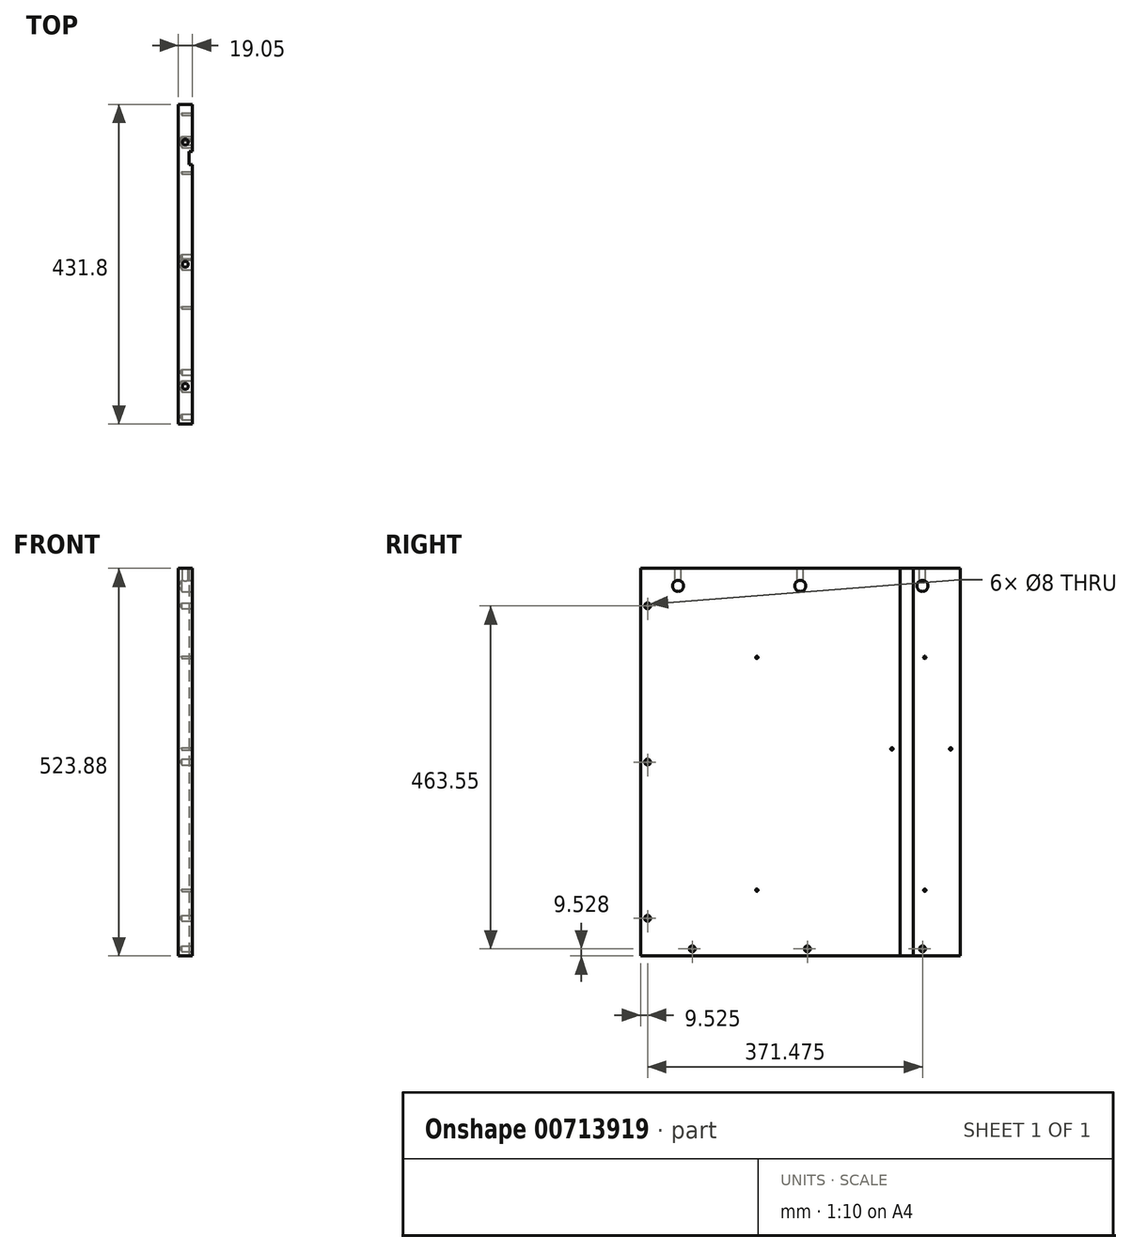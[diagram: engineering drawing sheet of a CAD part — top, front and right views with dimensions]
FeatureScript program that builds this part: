
annotation { "Feature Type Name" : "Feature", "Feature Type Description" : "" }
export const myFeature = defineFeature(function(context is Context, id is Id, definition is map)
    precondition{}
    {
        {
            var Q0;
            Q0=qCreatedBy(makeId("Right.planeOp"),FACE);
            var sketch = newSketch(context, id + "F0", { "sketchPlane" : qUnion([Q0])});
            skLineSegment(sketch, "E0.bottom", {"start": v(215.9, 261.94) * mm, "end": v(-215.9, 261.94) * mm});
            skLineSegment(sketch, "E0.top", {"start": v(215.9, -261.94) * mm, "end": v(-215.9, -261.94) * mm});
            skLineSegment(sketch, "E0.left", {"start": v(215.9, 261.94) * mm, "end": v(215.9, -261.94) * mm});
            skLineSegment(sketch, "E0.right", {"start": v(-215.9, 261.94) * mm, "end": v(-215.9, -261.94) * mm});
            skPoint(sketch, "E0.middle", {"position": v(0, 0) * mm});
            skSolve(sketch);
        }
        {
            var Q0;
            Q0=makeQuery(id+"F0.imprint","IMPRINT",FACE,{"disambiguationData":[TD([[makeQuery(id+"F0.imprint","IMPRINT",EDGE,{"derivedFrom":sQuery(id+"F0.wireOp",EDGE,"E0.bottom")}),1.0]])]});
            extrude(context, id + "F1", {"entities" : qUnion([Q0]), "depth" : 19.05 * mm, "offsetDistance" : 25.4 * mm});
        }
        {
            var Q0;
            Q0=makeQuery(id+"F1.opExtrude","CAP_FACE",FACE,{"disambiguationData":[OSD([sQuery(id+"F0.wireOp",EDGE,"E0.bottom"),sQuery(id+"F0.wireOp",EDGE,"E0.top"),sQuery(id+"F0.wireOp",EDGE,"E0.left"),sQuery(id+"F0.wireOp",EDGE,"E0.right")])],"isStart":false});
            var sketch = newSketch(context, id + "F2", { "sketchPlane" : qUnion([Q0])});
            skLineSegment(sketch, "E1", {"start": v(-215.9, 261.94) * mm, "end": v(-215.9, 238.06) * mm});
            skLineSegment(sketch, "E2", {"start": v(-215.9, 238.06) * mm, "end": v(215.9, 238.06) * mm});
            skLineSegment(sketch, "E3", {"start": v(215.9, 261.94) * mm, "end": v(206.38, 261.94) * mm});
            skPoint(sketch, "E4", {"position": v(206.38, 0) * mm});
            skPoint(sketch, "E5", {"position": v(206.38, -211.14) * mm});
            skLineSegment(sketch, "E6", {"start": v(-215.9, -261.94) * mm, "end": v(-215.9, -252.41) * mm});
            skLineSegment(sketch, "E7", {"start": v(-215.9, -252.41) * mm, "end": v(215.9, -252.41) * mm});
            skLineSegment(sketch, "E8", {"start": v(215.9, -252.41) * mm, "end": v(165.1, -252.41) * mm});
            skLineSegment(sketch, "E9", {"start": v(-215.9, -252.41) * mm, "end": v(-146.05, -252.41) * mm});
            skLineSegment(sketch, "E10", {"start": v(-215.9, -252.41) * mm, "end": v(-9.53, -252.41) * mm});
            skPoint(sketch, "E11", {"position": v(-146.05, -252.41) * mm});
            skPoint(sketch, "E12", {"position": v(-9.53, -252.41) * mm});
            skPoint(sketch, "E13", {"position": v(165.1, -252.41) * mm});
            skLineSegment(sketch, "E14", {"start": v(-215.9, 238.06) * mm, "end": v(-165.1, 238.06) * mm});
            skLineSegment(sketch, "E15", {"start": v(215.9, 238.06) * mm, "end": v(165.1, 238.06) * mm});
            skLineSegment(sketch, "E16", {"start": v(0, 238.06) * mm, "end": v(0, 261.94) * mm});
            skPoint(sketch, "E17", {"position": v(-165.1, 238.06) * mm});
            skPoint(sketch, "E18", {"position": v(0, 238.06) * mm});
            skPoint(sketch, "E19", {"position": v(165.1, 238.06) * mm});
            skLineSegment(sketch, "E20", {"start": v(215.9, -252.41) * mm, "end": v(9.52, -252.41) * mm});
            skPoint(sketch, "E21", {"position": v(9.52, -252.41) * mm});
            skLineSegment(sketch, "E22", {"start": v(-215.9, 261.94) * mm, "end": v(-206.38, 261.94) * mm});
            skLineSegment(sketch, "E23", {"start": v(-206.38, 261.94) * mm, "end": v(-206.38, -261.94) * mm});
            skLineSegment(sketch, "E24", {"start": v(-206.38, -261.94) * mm, "end": v(-206.38, -211.14) * mm});
            skLineSegment(sketch, "E25", {"start": v(-206.38, 261.94) * mm, "end": v(-206.38, 211.14) * mm});
            skLineSegment(sketch, "E26", {"start": v(-215.9, 0) * mm, "end": v(-206.38, 0) * mm});
            skPoint(sketch, "E27", {"position": v(-206.38, 211.14) * mm});
            skPoint(sketch, "E28", {"position": v(-206.38, 0) * mm});
            skPoint(sketch, "E29", {"position": v(-206.38, -211.14) * mm});
            skSolve(sketch);
        }
        {
            var Q0;
            Q0=sQuery(id+"F2.wireOp",VERTEX,"E27");
            var Q1;
            Q1=sQuery(id+"F2.wireOp",VERTEX,"E28");
            var Q2;
            Q2=sQuery(id+"F2.wireOp",VERTEX,"E29");
            var Q3;
            Q3=sQuery(id+"F2.wireOp",VERTEX,"E11");
            var Q4;
            Q4=sQuery(id+"F2.wireOp",VERTEX,"E21");
            var Q5;
            Q5=sQuery(id+"F2.wireOp",VERTEX,"E13");
            var Q6;
            Q6=makeQuery(id+"F1.opExtrude","SWEPT_BODY",BODY,{"disambiguationData":[OSD([sQuery(id+"F0.wireOp",EDGE,"E0.bottom"),sQuery(id+"F0.wireOp",EDGE,"E0.top"),sQuery(id+"F0.wireOp",EDGE,"E0.left"),sQuery(id+"F0.wireOp",EDGE,"E0.right")])]});
            hole(context, id + "F3", {"style" : HoleStyle.SIMPLE, "endStyle" : HoleEndStyle.BLIND, "holeDiameter" : 8 * mm, "majorDiameter" : 6.35 * mm, "holeDepth" : 14.22 * mm, "isTappedThrough" : true, "tappedDepth" : 12.7 * mm, "tapClearance" : 3, "startFromSketch" : true, "locations" : qUnion([Q0, Q1, Q2, Q3, Q4, Q5]), "scope" : qUnion([Q6])});
        }
        {
            var Q0;
            Q0=sQuery(id+"F2.wireOp",VERTEX,"E17");
            var Q1;
            Q1=sQuery(id+"F2.wireOp",VERTEX,"E18");
            var Q2;
            Q2=sQuery(id+"F2.wireOp",VERTEX,"E19");
            var Q3;
            Q3=makeQuery(id+"F1.opExtrude","SWEPT_BODY",BODY,{"disambiguationData":[OSD([sQuery(id+"F0.wireOp",EDGE,"E0.bottom"),sQuery(id+"F0.wireOp",EDGE,"E0.top"),sQuery(id+"F0.wireOp",EDGE,"E0.left"),sQuery(id+"F0.wireOp",EDGE,"E0.right")])]});
            hole(context, id + "F4", {"style" : HoleStyle.SIMPLE, "endStyle" : HoleEndStyle.BLIND, "holeDiameter" : 15 * mm, "majorDiameter" : 6.35 * mm, "holeDepth" : 14.22 * mm, "isTappedThrough" : true, "tappedDepth" : 12.7 * mm, "tapClearance" : 3, "startFromSketch" : true, "locations" : qUnion([Q0, Q1, Q2]), "scope" : qUnion([Q3])});
        }
        {
            var Q0;
            Q0=makeQuery(id+"F1.opExtrude","SWEPT_FACE",FACE,{"disambiguationData":[OSD([sQuery(id+"F0.wireOp",EDGE,"E0.bottom")])]});
            var sketch = newSketch(context, id + "F5", { "sketchPlane" : qUnion([Q0])});
            skLineSegment(sketch, "E30", {"start": v(9.53, 215.9) * mm, "end": v(9.53, 165.1) * mm});
            skLineSegment(sketch, "E31", {"start": v(9.53, -215.9) * mm, "end": v(9.53, -165.1) * mm});
            skLineSegment(sketch, "E32", {"start": v(19.05, 0) * mm, "end": v(9.52, 0) * mm});
            skPoint(sketch, "E33", {"position": v(9.53, 165.1) * mm});
            skPoint(sketch, "E34", {"position": v(9.52, 0) * mm});
            skPoint(sketch, "E35", {"position": v(9.53, -165.1) * mm});
            skSolve(sketch);
        }
        {
            var Q0;
            Q0=sQuery(id+"F5.wireOp",VERTEX,"E33");
            var Q1;
            Q1=sQuery(id+"F5.wireOp",VERTEX,"E34");
            var Q2;
            Q2=sQuery(id+"F5.wireOp",VERTEX,"E35");
            var Q3;
            Q3=makeQuery(id+"F1.opExtrude","SWEPT_BODY",BODY,{"disambiguationData":[OSD([sQuery(id+"F0.wireOp",EDGE,"E0.bottom"),sQuery(id+"F0.wireOp",EDGE,"E0.top"),sQuery(id+"F0.wireOp",EDGE,"E0.left"),sQuery(id+"F0.wireOp",EDGE,"E0.right")])]});
            hole(context, id + "F6", {"style" : HoleStyle.SIMPLE, "endStyle" : HoleEndStyle.BLIND, "holeDiameter" : 8 * mm, "majorDiameter" : 6.35 * mm, "holeDepth" : 25.4 * mm, "isTappedThrough" : true, "tappedDepth" : 12.7 * mm, "tapClearance" : 3, "startFromSketch" : true, "locations" : qUnion([Q0, Q1, Q2]), "scope" : qUnion([Q3])});
        }
        {
            var Q0;
            Q0=makeQuery(id+"F1.opExtrude","CAP_FACE",FACE,{"disambiguationData":[OSD([sQuery(id+"F0.wireOp",EDGE,"E0.bottom"),sQuery(id+"F0.wireOp",EDGE,"E0.top"),sQuery(id+"F0.wireOp",EDGE,"E0.left"),sQuery(id+"F0.wireOp",EDGE,"E0.right")])],"isStart":false});
            var sketch = newSketch(context, id + "F7", { "sketchPlane" : qUnion([Q0])});
            skLineSegment(sketch, "E36", {"start": v(-215.9, -261.94) * mm, "end": v(-215.9, -173.04) * mm});
            skLineSegment(sketch, "E37", {"start": v(-215.9, -261.94) * mm, "end": v(-215.9, 141.41) * mm});
            skLineSegment(sketch, "E38", {"start": v(-215.9, -261.94) * mm, "end": v(-215.9, 17.72) * mm});
            skLineSegment(sketch, "E39", {"start": v(215.9, -261.94) * mm, "end": v(215.9, -173.04) * mm});
            skLineSegment(sketch, "E40", {"start": v(215.9, -173.04) * mm, "end": v(-58.74, -173.04) * mm});
            skLineSegment(sketch, "E41", {"start": v(215.9, -173.04) * mm, "end": v(168.27, -173.04) * mm});
            skLineSegment(sketch, "E42", {"start": v(215.9, -261.94) * mm, "end": v(215.9, 141.41) * mm});
            skLineSegment(sketch, "E43", {"start": v(215.9, 141.41) * mm, "end": v(-58.74, 141.41) * mm});
            skLineSegment(sketch, "E44", {"start": v(215.9, 141.41) * mm, "end": v(168.28, 141.41) * mm});
            skLineSegment(sketch, "E45", {"start": v(215.9, -261.94) * mm, "end": v(215.9, 17.72) * mm});
            skLineSegment(sketch, "E46", {"start": v(215.9, 17.72) * mm, "end": v(123.82, 17.72) * mm});
            skLineSegment(sketch, "E47", {"start": v(215.9, 17.72) * mm, "end": v(203.2, 17.72) * mm});
            skPoint(sketch, "E48", {"position": v(168.28, 141.41) * mm});
            skPoint(sketch, "E49", {"position": v(-58.74, 141.41) * mm});
            skPoint(sketch, "E50", {"position": v(203.2, 17.72) * mm});
            skPoint(sketch, "E51", {"position": v(123.82, 17.72) * mm});
            skPoint(sketch, "E52", {"position": v(168.27, -173.04) * mm});
            skPoint(sketch, "E53", {"position": v(-58.74, -173.04) * mm});
            skSolve(sketch);
        }
        {
            var Q0;
            Q0=sQuery(id+"F7.wireOp",VERTEX,"E49");
            var Q1;
            Q1=sQuery(id+"F7.wireOp",VERTEX,"E48");
            var Q2;
            Q2=sQuery(id+"F7.wireOp",VERTEX,"E51");
            var Q3;
            Q3=sQuery(id+"F7.wireOp",VERTEX,"E50");
            var Q4;
            Q4=sQuery(id+"F7.wireOp",VERTEX,"E52");
            var Q5;
            Q5=sQuery(id+"F7.wireOp",VERTEX,"E53");
            var Q6;
            Q6=makeQuery(id+"F1.opExtrude","SWEPT_BODY",BODY,{"disambiguationData":[OSD([sQuery(id+"F0.wireOp",EDGE,"E0.bottom"),sQuery(id+"F0.wireOp",EDGE,"E0.top"),sQuery(id+"F0.wireOp",EDGE,"E0.left"),sQuery(id+"F0.wireOp",EDGE,"E0.right")])]});
            hole(context, id + "F8", {"style" : HoleStyle.SIMPLE, "endStyle" : HoleEndStyle.BLIND, "holeDiameter" : 3.17 * mm, "majorDiameter" : 6.35 * mm, "holeDepth" : 14.22 * mm, "isTappedThrough" : true, "tappedDepth" : 12.7 * mm, "tapClearance" : 3, "startFromSketch" : true, "locations" : qUnion([Q0, Q1, Q2, Q3, Q4, Q5]), "scope" : qUnion([Q6])});
        }
        {
            var Q0;
            Q0=makeQuery(id+"F1.opExtrude","CAP_FACE",FACE,{"disambiguationData":[OSD([sQuery(id+"F0.wireOp",EDGE,"E0.bottom"),sQuery(id+"F0.wireOp",EDGE,"E0.top"),sQuery(id+"F0.wireOp",EDGE,"E0.left"),sQuery(id+"F0.wireOp",EDGE,"E0.right")])],"isStart":false});
            var sketch = newSketch(context, id + "F9", { "sketchPlane" : qUnion([Q0])});
            skLineSegment(sketch, "E54", {"start": v(-215.9, 261.94) * mm, "end": v(134.87, 261.94) * mm});
            skLineSegment(sketch, "E55.bottom", {"start": v(134.87, 261.94) * mm, "end": v(152.4, 261.94) * mm});
            skLineSegment(sketch, "E55.top", {"start": v(134.87, -261.94) * mm, "end": v(152.4, -261.94) * mm});
            skLineSegment(sketch, "E55.left", {"start": v(134.87, 261.94) * mm, "end": v(134.87, -261.94) * mm});
            skLineSegment(sketch, "E55.right", {"start": v(152.4, 261.94) * mm, "end": v(152.4, -261.94) * mm});
            skLineSegment(sketch, "E56", {"start": v(152.4, 261.94) * mm, "end": v(215.9, 261.94) * mm});
            skSolve(sketch);
        }
        {
            var Q0;
            Q0=makeQuery(id+"F9.imprint","IMPRINT",FACE,{"disambiguationData":[TD([[makeQuery(id+"F9.imprint","IMPRINT",EDGE,{"derivedFrom":sQuery(id+"F9.wireOp",EDGE,"E55.bottom")}),1.0]])]});
            extrude(context, id + "F10", {"entities" : qUnion([Q0]), "operationType" : NewBodyOperationType.REMOVE, "oppositeDirection" : true, "depth" : 4.83 * mm, "offsetDistance" : 25.4 * mm});
        }
    });
